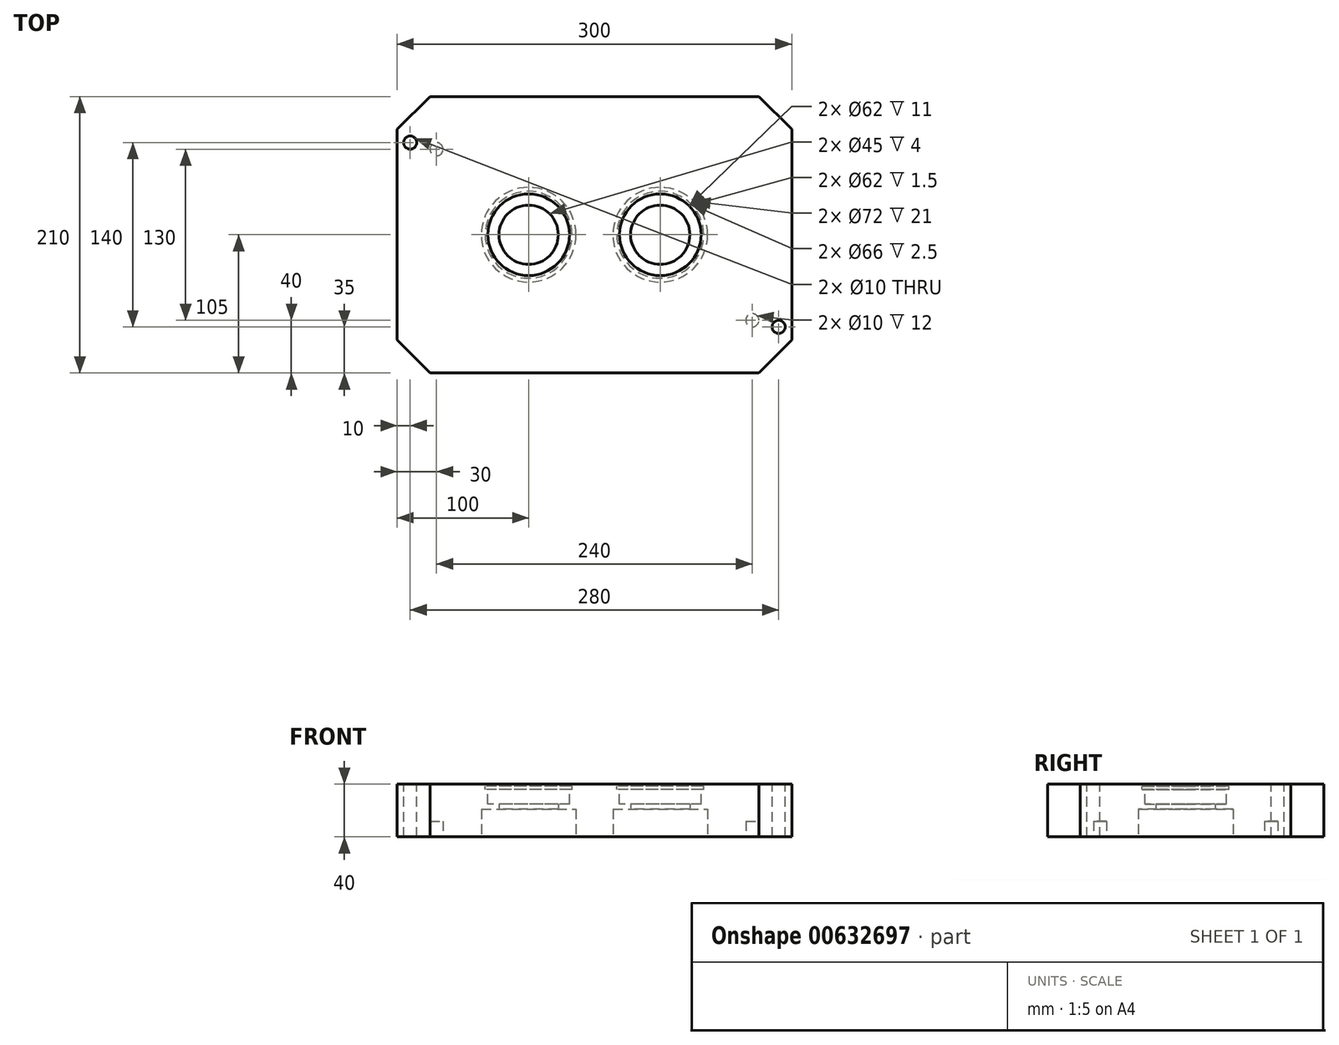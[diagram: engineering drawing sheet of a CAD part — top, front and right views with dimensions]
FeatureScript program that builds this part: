
annotation { "Feature Type Name" : "Feature", "Feature Type Description" : "" }
export const myFeature = defineFeature(function(context is Context, id is Id, definition is map)
    precondition{}
    {
        {
            var Q0;
            Q0=qCreatedBy(makeId("Top.planeOp"),FACE);
            var sketch = newSketch(context, id + "F0", { "sketchPlane" : qUnion([Q0])});
            skLineSegment(sketch, "E0.bottom", {"start": v(-150, 105) * mm, "end": v(150, 105) * mm});
            skLineSegment(sketch, "E0.top", {"start": v(-150, -105) * mm, "end": v(150, -105) * mm});
            skLineSegment(sketch, "E0.left", {"start": v(-150, 105) * mm, "end": v(-150, -105) * mm});
            skLineSegment(sketch, "E0.right", {"start": v(150, 105) * mm, "end": v(150, -105) * mm});
            skCircle(sketch, "E1", {"center": v(-50, 0) * mm, "radius": 22.5 * mm});
            skCircle(sketch, "E2", {"center": v(50, 0) * mm, "radius": 22.5 * mm});
            skSolve(sketch);
        }
        {
            var Q0;
            Q0=makeQuery(id+"F0.imprint","IMPRINT",FACE,{"disambiguationData":[TD([[makeQuery(id+"F0.imprint","IMPRINT",EDGE,{"derivedFrom":sQuery(id+"F0.wireOp",EDGE,"E0.bottom")}),-1.0]])]});
            extrude(context, id + "F1", {"entities" : qUnion([Q0]), "depth" : 40 * mm, "offsetDistance" : 25 * mm});
        }
        {
            var Q0;
            Q0=makeQuery(id+"F1.opExtrude","CAP_FACE",FACE,{"disambiguationData":[OSD([sQuery(id+"F0.wireOp",EDGE,"E0.bottom"),sQuery(id+"F0.wireOp",EDGE,"E0.top"),sQuery(id+"F0.wireOp",EDGE,"E0.left"),sQuery(id+"F0.wireOp",EDGE,"E0.right"),sQuery(id+"F0.wireOp",EDGE,"E1"),sQuery(id+"F0.wireOp",EDGE,"E2")])],"isStart":false});
            var sketch = newSketch(context, id + "F2", { "sketchPlane" : qUnion([Q0])});
            skCircle(sketch, "E3", {"center": v(-50, 0) * mm, "radius": 31 * mm});
            skCircle(sketch, "E4", {"center": v(50, 0) * mm, "radius": 31 * mm});
            skSolve(sketch);
        }
        {
            var Q0;
            Q0=makeQuery(id+"F2.imprint","IMPRINT",FACE,{"disambiguationData":[TD([[makeQuery(id+"F2.imprint","IMPRINT",EDGE,{"derivedFrom":sQuery(id+"F2.wireOp",EDGE,"E3")}),1.0]])]});
            var Q1;
            Q1=makeQuery(id+"F2.imprint","IMPRINT",FACE,{"disambiguationData":[TD([[makeQuery(id+"F2.imprint","IMPRINT",EDGE,{"derivedFrom":sQuery(id+"F2.wireOp",EDGE,"E4")}),1.0]])]});
            extrude(context, id + "F3", {"entities" : qUnion([Q0, Q1]), "operationType" : NewBodyOperationType.REMOVE, "oppositeDirection" : true, "depth" : 15 * mm, "offsetDistance" : 25 * mm});
        }
        {
            var Q0;
            Q0=makeQuery(id+"F1.opExtrude","CAP_FACE",FACE,{"disambiguationData":[OSD([sQuery(id+"F0.wireOp",EDGE,"E0.bottom"),sQuery(id+"F0.wireOp",EDGE,"E0.top"),sQuery(id+"F0.wireOp",EDGE,"E0.left"),sQuery(id+"F0.wireOp",EDGE,"E0.right"),sQuery(id+"F0.wireOp",EDGE,"E1"),sQuery(id+"F0.wireOp",EDGE,"E2")])],"isStart":true});
            var sketch = newSketch(context, id + "F4", { "sketchPlane" : qUnion([Q0])});
            skCircle(sketch, "E5", {"center": v(-50, 0) * mm, "radius": 36 * mm});
            skCircle(sketch, "E6", {"center": v(50, 0) * mm, "radius": 36 * mm});
            skSolve(sketch);
        }
        {
            var Q0;
            Q0=makeQuery(id+"F4.imprint","IMPRINT",FACE,{"disambiguationData":[TD([[makeQuery(id+"F4.imprint","IMPRINT",EDGE,{"derivedFrom":sQuery(id+"F4.wireOp",EDGE,"E5")}),1.0]])]});
            var Q1;
            Q1=makeQuery(id+"F4.imprint","IMPRINT",FACE,{"disambiguationData":[TD([[makeQuery(id+"F4.imprint","IMPRINT",EDGE,{"derivedFrom":sQuery(id+"F4.wireOp",EDGE,"E6")}),1.0]])]});
            extrude(context, id + "F5", {"entities" : qUnion([Q0, Q1]), "operationType" : NewBodyOperationType.REMOVE, "oppositeDirection" : true, "depth" : 21 * mm, "offsetDistance" : 25 * mm});
        }
        {
            var Q0;
            Q0=qCreatedBy(makeId("Top.planeOp"),FACE);
            cPlane(context, id + "F6", {"entities" : qUnion([Q0]), "cplaneType" : CPlaneType.OFFSET, "offset" : 38.5 * mm, "width" : 150 * mm, "height" : 150 * mm});
        }
        {
            var Q0;
            Q0=qCreatedBy(id+"F6.planeOp",FACE);
            var sketch = newSketch(context, id + "F7", { "sketchPlane" : qUnion([Q0])});
            skCircle(sketch, "E7", {"center": v(-50, 0) * mm, "radius": 33 * mm});
            skCircle(sketch, "E8", {"center": v(50, 0) * mm, "radius": 33 * mm});
            skSolve(sketch);
        }
        {
            var Q0;
            Q0=makeQuery(id+"F7.imprint","IMPRINT",FACE,{"disambiguationData":[TD([[makeQuery(id+"F7.imprint","IMPRINT",EDGE,{"derivedFrom":sQuery(id+"F7.wireOp",EDGE,"E7")}),1.0]])]});
            var Q1;
            Q1=makeQuery(id+"F7.imprint","IMPRINT",FACE,{"disambiguationData":[TD([[makeQuery(id+"F7.imprint","IMPRINT",EDGE,{"derivedFrom":sQuery(id+"F7.wireOp",EDGE,"E8")}),1.0]])]});
            extrude(context, id + "F8", {"entities" : qUnion([Q0, Q1]), "operationType" : NewBodyOperationType.REMOVE, "oppositeDirection" : true, "depth" : 2.5 * mm, "offsetDistance" : 25 * mm});
        }
        {
            var Q0;
            Q0=makeQuery(id+"F1.opExtrude","CAP_FACE",FACE,{"disambiguationData":[OSD([sQuery(id+"F0.wireOp",EDGE,"E0.bottom"),sQuery(id+"F0.wireOp",EDGE,"E0.top"),sQuery(id+"F0.wireOp",EDGE,"E0.left"),sQuery(id+"F0.wireOp",EDGE,"E0.right"),sQuery(id+"F0.wireOp",EDGE,"E1"),sQuery(id+"F0.wireOp",EDGE,"E2")])],"isStart":false});
            var sketch = newSketch(context, id + "F9", { "sketchPlane" : qUnion([Q0])});
            skCircle(sketch, "E9", {"center": v(-140, 70) * mm, "radius": 5 * mm});
            skCircle(sketch, "E10", {"center": v(140, -70) * mm, "radius": 5 * mm});
            skCircle(sketch, "E11", {"center": v(-70, 95) * mm, "radius": 4 * mm});
            skCircle(sketch, "E12", {"center": v(70, 95) * mm, "radius": 4 * mm});
            skCircle(sketch, "E13", {"center": v(140, 50) * mm, "radius": 4 * mm});
            skCircle(sketch, "E14", {"center": v(140, -50) * mm, "radius": 4 * mm});
            skCircle(sketch, "E15", {"center": v(70, -95) * mm, "radius": 4 * mm});
            skCircle(sketch, "E16", {"center": v(-70, -95) * mm, "radius": 4 * mm});
            skCircle(sketch, "E17", {"center": v(-140, -50) * mm, "radius": 4 * mm});
            skCircle(sketch, "E18", {"center": v(-140, 50) * mm, "radius": 4 * mm});
            skSolve(sketch);
        }
        {
            var Q0;
            Q0=makeQuery(id+"F9.imprint","IMPRINT",FACE,{"disambiguationData":[TD([[makeQuery(id+"F9.imprint","IMPRINT",EDGE,{"derivedFrom":sQuery(id+"F9.wireOp",EDGE,"E9")}),1.0]])]});
            var Q1;
            Q1=makeQuery(id+"F9.imprint","IMPRINT",FACE,{"disambiguationData":[TD([[makeQuery(id+"F9.imprint","IMPRINT",EDGE,{"derivedFrom":sQuery(id+"F9.wireOp",EDGE,"E10")}),1.0]])]});
            extrude(context, id + "F10", {"entities" : qUnion([Q0, Q1]), "operationType" : NewBodyOperationType.REMOVE, "oppositeDirection" : true, "depth" : 40 * mm, "offsetDistance" : 25 * mm});
        }
        {
            var Q0;
            Q0=makeQuery(id+"F1.opExtrude","SWEPT_EDGE",EDGE,{"disambiguationData":[OSD([sQuery(id+"F0.wireOp",EDGE,"E0.top"),sQuery(id+"F0.wireOp",EDGE,"E0.right")])]});
            var Q1;
            Q1=makeQuery(id+"F1.opExtrude","SWEPT_EDGE",EDGE,{"disambiguationData":[OSD([sQuery(id+"F0.wireOp",EDGE,"E0.top"),sQuery(id+"F0.wireOp",EDGE,"E0.left")])]});
            var Q2;
            Q2=makeQuery(id+"F1.opExtrude","SWEPT_EDGE",EDGE,{"disambiguationData":[OSD([sQuery(id+"F0.wireOp",EDGE,"E0.bottom"),sQuery(id+"F0.wireOp",EDGE,"E0.right")])]});
            var Q3;
            Q3=makeQuery(id+"F1.opExtrude","SWEPT_EDGE",EDGE,{"disambiguationData":[OSD([sQuery(id+"F0.wireOp",EDGE,"E0.bottom"),sQuery(id+"F0.wireOp",EDGE,"E0.left")])]});
            chamfer(context, id + "F11", {"entities" : qUnion([Q0, Q1, Q2, Q3]), "width" : 25 * mm, "tangentPropagation" : true});
        }
        {
            var Q0;
            Q0=makeQuery(id+"F1.opExtrude","CAP_FACE",FACE,{"disambiguationData":[OSD([sQuery(id+"F0.wireOp",EDGE,"E0.bottom"),sQuery(id+"F0.wireOp",EDGE,"E0.top"),sQuery(id+"F0.wireOp",EDGE,"E0.left"),sQuery(id+"F0.wireOp",EDGE,"E0.right"),sQuery(id+"F0.wireOp",EDGE,"E1"),sQuery(id+"F0.wireOp",EDGE,"E2")])],"isStart":true});
            var sketch = newSketch(context, id + "F12", { "sketchPlane" : qUnion([Q0])});
            skCircle(sketch, "E19", {"center": v(-130, 0) * mm, "radius": 4 * mm});
            skCircle(sketch, "E20", {"center": v(0, -80) * mm, "radius": 4 * mm});
            skCircle(sketch, "E21", {"center": v(130, 0) * mm, "radius": 4 * mm});
            skCircle(sketch, "E22", {"center": v(0, 80) * mm, "radius": 4 * mm});
            skArc(sketch, "E23", {"start": v(81.59, -28.06) * mm, "mid": v(92.25, 0) * mm, "end": v(81.59, 28.06) * mm});
            skArc(sketch, "E24", {"start": v(-18.41, -28.06) * mm, "mid": v(-7.75, 0) * mm, "end": v(-18.41, 28.06) * mm});
            skCircle(sketch, "E25", {"center": v(20.12, 29.88) * mm, "radius": 2.5 * mm});
            skCircle(sketch, "E26", {"center": v(-79.88, 29.88) * mm, "radius": 2.5 * mm});
            skCircle(sketch, "E27.1.0", {"center": v(20.12, -29.88) * mm, "radius": 2.5 * mm});
            skCircle(sketch, "E27.2.0", {"center": v(79.88, -29.88) * mm, "radius": 2.5 * mm});
            skCircle(sketch, "E27.3.0", {"center": v(79.88, 29.88) * mm, "radius": 2.5 * mm});
            skCircle(sketch, "E28.1.0", {"center": v(-79.88, -29.88) * mm, "radius": 2.5 * mm});
            skCircle(sketch, "E28.2.0", {"center": v(-20.12, -29.88) * mm, "radius": 2.5 * mm});
            skCircle(sketch, "E28.3.0", {"center": v(-20.12, 29.88) * mm, "radius": 2.5 * mm});
            skArc(sketch, "E29.trimOffspring", {"start": v(78.06, 31.59) * mm, "mid": v(50, 42.25) * mm, "end": v(21.94, 31.59) * mm});
            skArc(sketch, "E30.trimOffspring", {"start": v(18.41, 28.06) * mm, "mid": v(7.75, 0) * mm, "end": v(18.41, -28.06) * mm});
            skArc(sketch, "E31.trimOffspring", {"start": v(21.94, -31.59) * mm, "mid": v(50, -42.25) * mm, "end": v(78.06, -31.59) * mm});
            skArc(sketch, "E32.trimOffspring", {"start": v(-21.94, 31.59) * mm, "mid": v(-50, 42.25) * mm, "end": v(-78.06, 31.59) * mm});
            skArc(sketch, "E33.trimOffspring", {"start": v(-81.59, 28.06) * mm, "mid": v(-92.25, 0) * mm, "end": v(-81.59, -28.06) * mm});
            skArc(sketch, "E34.trimOffspring", {"start": v(-78.06, -31.59) * mm, "mid": v(-50, -42.25) * mm, "end": v(-21.94, -31.59) * mm});
            skCircle(sketch, "E35", {"center": v(120, 65) * mm, "radius": 5 * mm});
            skCircle(sketch, "E36", {"center": v(-120, -65) * mm, "radius": 5 * mm});
            skSolve(sketch);
        }
        {
            var Q0;
            Q0=makeQuery(id+"F12.imprint","IMPRINT",FACE,{"disambiguationData":[TD([[makeQuery(id+"F12.imprint","IMPRINT",EDGE,{"derivedFrom":sQuery(id+"F12.wireOp",EDGE,"E35")}),1.0]])]});
            var Q1;
            Q1=makeQuery(id+"F12.imprint","IMPRINT",FACE,{"disambiguationData":[TD([[makeQuery(id+"F12.imprint","IMPRINT",EDGE,{"derivedFrom":sQuery(id+"F12.wireOp",EDGE,"E36")}),1.0]])]});
            extrude(context, id + "F13", {"entities" : qUnion([Q0, Q1]), "operationType" : NewBodyOperationType.REMOVE, "oppositeDirection" : true, "depth" : 12 * mm, "offsetDistance" : 25 * mm});
        }
    });
